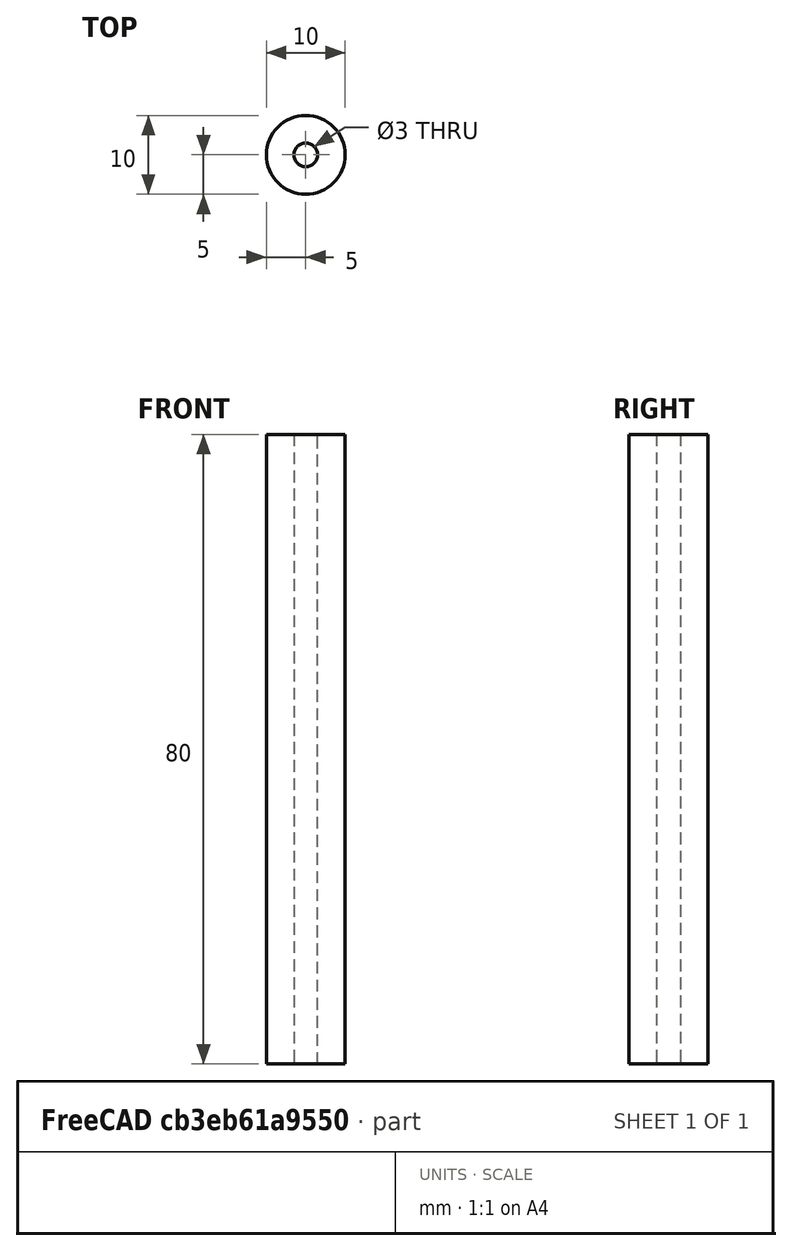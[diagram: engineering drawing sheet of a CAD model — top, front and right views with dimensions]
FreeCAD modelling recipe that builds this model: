
FCSTD DOCUMENT  (FreeCAD 1.0R39109 (Git))
Label: One Hitter
License: Creative Commons Attribution 4.0
LicenseURL: https://creativecommons.org/licenses/by/4.0/
objects: Sketcher::SketchObject×2, PartDesign::Body×2, App::Part×2, Spreadsheet::Sheet×1, PartDesign::Pad×1
note: 9 computed .brp shape members not serialized (recipe doc carries the construction recipe); baked Part::Feature solids carry a one-line shape summary decoded from their .brp

FEATURE [Spreadsheet::Sheet] Spreadsheet  label="config"
  cells = A2='pipeOD; B2(pipeOD)=10; A3='pipeID; B3(pipeID)=3; A4='pipeLength; B4(pipeLength)=80; A5='dugoutWidth; B5(dugoutWidth)=50; A6='dugoutBottomThickness; B6(dugoutBottomThickness)=5; A7='dugoutTopThickness; B7(dugoutTopThickness)=5; A8='dugoutSealThickness; B8(dugoutSealThickness)=2; A9='dugoutWallThickness; B9(dugoutWallThickness)=2
FEATURE [Sketcher::SketchObject] Sketch
  ArcFitTolerance = 1e-06
  AttachmentSupport = -> [XY_Plane001]
  FullyConstrained = true
  MakeInternals = false
  MapMode = 5
  expr: Constraints[0] = <<config>>.pipeID
  expr: Constraints[2] = <<config>>.pipeOD
  sketch-geometry (4):
    g0: Circle CenterX=0 CenterY=0 CenterZ=0 NormalX=0 NormalY=0 NormalZ=1 AngleXU=0 Radius=1.5
    g1: Circle CenterX=0 CenterY=0 CenterZ=0 NormalX=0 NormalY=0 NormalZ=1 AngleXU=0 Radius=5
    g2: GeomPoint X=0 Y=0 Z=0
    g3: GeomPoint X=0 Y=0 Z=0
  constraints (6):
    c: Diameter(g0) = 3
    c: Coincident(g0,g-1)
    c: Diameter(g1) = 10
    c: Coincident(g1,g0)
    c: Coincident(g2,g0)
    c: Coincident(g0,g3)
FEATURE [PartDesign::Pad] Pad
  Direction = (0,0,1)
  Length = 80
  Length2 = 10
  Profile = -> Sketch
  ReferenceAxis = -> Sketch [N_Axis]
  Suppressed = false
  Type = 0
  expr: Length = <<config>>.pipeLength
FEATURE [PartDesign::Body] Body  label="Pipe Body"
  AllowCompound = false
  Group = -> [Sketch,Pad]
  Origin = -> Origin001
  Tip = -> Pad
FEATURE [App::Part] Part  label="Pipe"
  Group = -> [Body]
  Origin = -> Origin
FEATURE [Sketcher::SketchObject] Sketch001
  ArcFitTolerance = 1e-06
  AttachmentSupport = -> [XZ_Plane003]
  FullyConstrained = true
  MakeInternals = false
  MapMode = 5
  Placement = pos=(0,0,0) rot=(1,0,0;1.5708rad)
  expr: Constraints[10] = <<config>>.pipeOD / 2 + <<config>>.dugoutWallThickness
  expr: Constraints[11] = <<config>>.dugoutBottomThickness
  expr: Constraints[8] = <<config>>.pipeLength + <<config>>.dugoutTopThickness + <<config>>.dugoutBottomThickness
  expr: Constraints[9] = <<config>>.dugoutWidth
  sketch-geometry (4):
    g0: LineSegment StartX=-7 StartY=85 StartZ=0 EndX=-7 EndY=-5 EndZ=0
    g1: LineSegment StartX=-7 StartY=-5 StartZ=0 EndX=43 EndY=-5 EndZ=0
    g2: LineSegment StartX=43 StartY=-5 StartZ=0 EndX=43 EndY=85 EndZ=0
    g3: LineSegment StartX=43 StartY=85 StartZ=0 EndX=-7 EndY=85 EndZ=0
  constraints (12):
    c: Coincident(g0,g1)
    c: Coincident(g1,g2)
    c: Coincident(g2,g3)
    c: Coincident(g3,g0)
    c: Vertical(g0)
    c: Vertical(g2)
    c: Horizontal(g1)
    c: Horizontal(g3)
    c: DistanceY(g0,g0) = 90
    c: DistanceX(g3,g3) = 50
    c: DistanceX(g0,g-1) = 7
    c: DistanceY(g0,g-1) = 5
FEATURE [PartDesign::Body] Body001  label="Dugout Body"
  AllowCompound = false
  Group = -> [Sketch001]
  Origin = -> Origin003
FEATURE [App::Part] Part001  label="Dugout"
  Group = -> [Body001]
  Origin = -> Origin002
